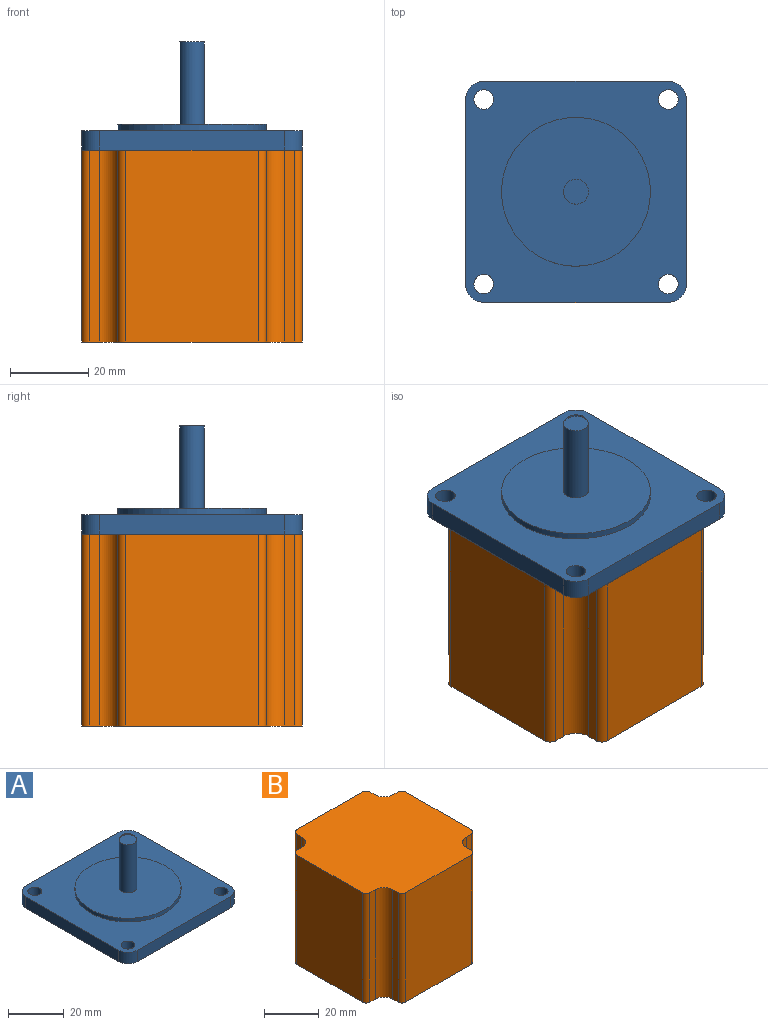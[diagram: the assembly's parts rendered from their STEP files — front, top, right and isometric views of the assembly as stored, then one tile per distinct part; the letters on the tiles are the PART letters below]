
ASSEMBLY  parts=2 mates=1
PART A: 18 faces, bbox 56.4x56.4x27.6 mm
  f0: plane 38x38mm, normal (0,0,1), area 1102.4mm2, adj f15,f16
  f1: plane 56.4x56.4mm, normal (0,0,1), area 1949.9mm2, adj f2,f3,f4,f5,f6,f7,f8,f9
  f2: cylinder r=4.63mm len=5mm, axis (0,0,1), area 36.4mm2, adj f1,f3,f9,f10
  f3: plane 47.14x5mm, normal (1,0,0), area 235.7mm2, adj f1,f2,f4,f10
  f4: cylinder r=4.63mm len=5mm, axis (0,0,1), area 36.4mm2, adj f1,f3,f5,f10
  f5: plane 47.14x5mm, normal (0,-1,0), area 235.7mm2, adj f1,f4,f6,f10
  f6: cylinder r=4.63mm len=5mm, axis (0,0,1), area 36.4mm2, adj f1,f5,f7,f10
  f7: plane 47.14x5mm, normal (-1,0,0), area 235.7mm2, adj f1,f6,f8,f10
  f8: cylinder r=4.63mm len=5mm, axis (0,0,1), area 36.4mm2, adj f1,f7,f9,f10
  f9: plane 47.14x5mm, normal (0,1,0), area 235.7mm2, adj f1,f2,f8,f10
  f10: plane 56.4x56.4mm, normal (0,0,-1), area 3084mm2, adj f2,f3,f4,f5,f6,f7,f8,f9
  f11: cylinder r=2.5mm len=5mm, axis (0,0,1), area 78.5mm2, adj f1,f10
  f12: cylinder r=2.5mm len=5mm, axis (0,0,1), area 78.5mm2, adj f1,f10
  f13: cylinder r=2.5mm len=5mm, axis (0,0,1), area 78.5mm2, adj f1,f10
  f14: cylinder r=2.5mm len=5mm, axis (0,0,1), area 78.5mm2, adj f1,f10
  f15: cylinder r=19mm len=38mm, axis (0,0,-1), area 191mm2, adj f0,f1
  f16: cylinder r=3.17mm len=21mm, axis (0,0,-1), area 418.9mm2, adj f0,f17
  f17: plane 6.35x6.35mm, normal (0,0,1), area 31.7mm2, adj f16
PART B: 26 faces, bbox 56.4x56.4x49 mm
  f0: cylinder r=2mm len=49mm, axis (0,0,1), area 153.9mm2, adj f1,f23,f24,f25
  f1: plane 49x2.63mm, normal (0,-1,0), area 128.9mm2, adj f0,f2,f24,f25
  f2: cylinder r=4.63mm len=49mm, axis (0,0,1), area 356.4mm2, adj f1,f3,f24,f25
  f3: plane 49x2.63mm, normal (1,0,0), area 128.9mm2, adj f2,f4,f24,f25
  f4: cylinder r=2mm len=49mm, axis (0,0,1), area 153.9mm2, adj f3,f5,f24,f25
  f5: plane 49x33.88mm, normal (0,-1,0), area 1660.1mm2, adj f4,f6,f24,f25
  f6: cylinder r=2mm len=49mm, axis (0,0,1), area 153.9mm2, adj f5,f7,f24,f25
  f7: plane 49x2.63mm, normal (-1,0,0), area 128.9mm2, adj f6,f8,f24,f25
  f8: cylinder r=4.63mm len=49mm, axis (0,0,1), area 356.4mm2, adj f7,f9,f24,f25
  f9: plane 49x2.63mm, normal (0,-1,0), area 128.9mm2, adj f8,f10,f24,f25
  f10: cylinder r=2mm len=49mm, axis (0,0,1), area 153.9mm2, adj f9,f11,f24,f25
  f11: plane 49x33.88mm, normal (-1,0,0), area 1660.1mm2, adj f10,f12,f24,f25
  f12: cylinder r=2mm len=49mm, axis (0,0,1), area 153.9mm2, adj f11,f13,f24,f25
  f13: plane 49x2.63mm, normal (0,1,0), area 128.9mm2, adj f12,f14,f24,f25
  f14: cylinder r=4.63mm len=49mm, axis (0,0,1), area 356.4mm2, adj f13,f15,f24,f25
  f15: plane 49x2.63mm, normal (-1,0,0), area 128.9mm2, adj f14,f16,f24,f25
  f16: cylinder r=2mm len=49mm, axis (0,0,1), area 153.9mm2, adj f15,f17,f24,f25
  f17: plane 49x33.88mm, normal (0,1,0), area 1660.1mm2, adj f16,f18,f24,f25
  f18: cylinder r=2mm len=49mm, axis (0,0,1), area 153.9mm2, adj f17,f19,f24,f25
  f19: plane 49x2.63mm, normal (1,0,0), area 128.9mm2, adj f18,f20,f24,f25
  f20: cylinder r=4.63mm len=49mm, axis (0,0,1), area 356.4mm2, adj f19,f21,f24,f25
  f21: plane 49x2.63mm, normal (0,1,0), area 128.9mm2, adj f20,f22,f24,f25
  f22: cylinder r=2mm len=49mm, axis (0,0,1), area 153.9mm2, adj f21,f23,f24,f25
  f23: plane 49x33.88mm, normal (1,0,0), area 1660.1mm2, adj f0,f22,f24,f25
  f24: plane 56.4x56.4mm, normal (0,0,-1), area 2849.5mm2, adj f0,f1,f2,f3,f4,f5,f6,f7
  f25: plane 56.4x56.4mm, normal (0,0,1), area 2849.5mm2, adj f0,f1,f2,f3,f4,f5,f6,f7
PLACE A t=(-12.54,-11.03,10.02)mm
PLACE B t=(-12.54,-11.03,10.02)mm fixed
MATE fastened A.f6 <-> B.f8  axis (0,0,-1) through (-36.11,-34.6,5.02)mm
